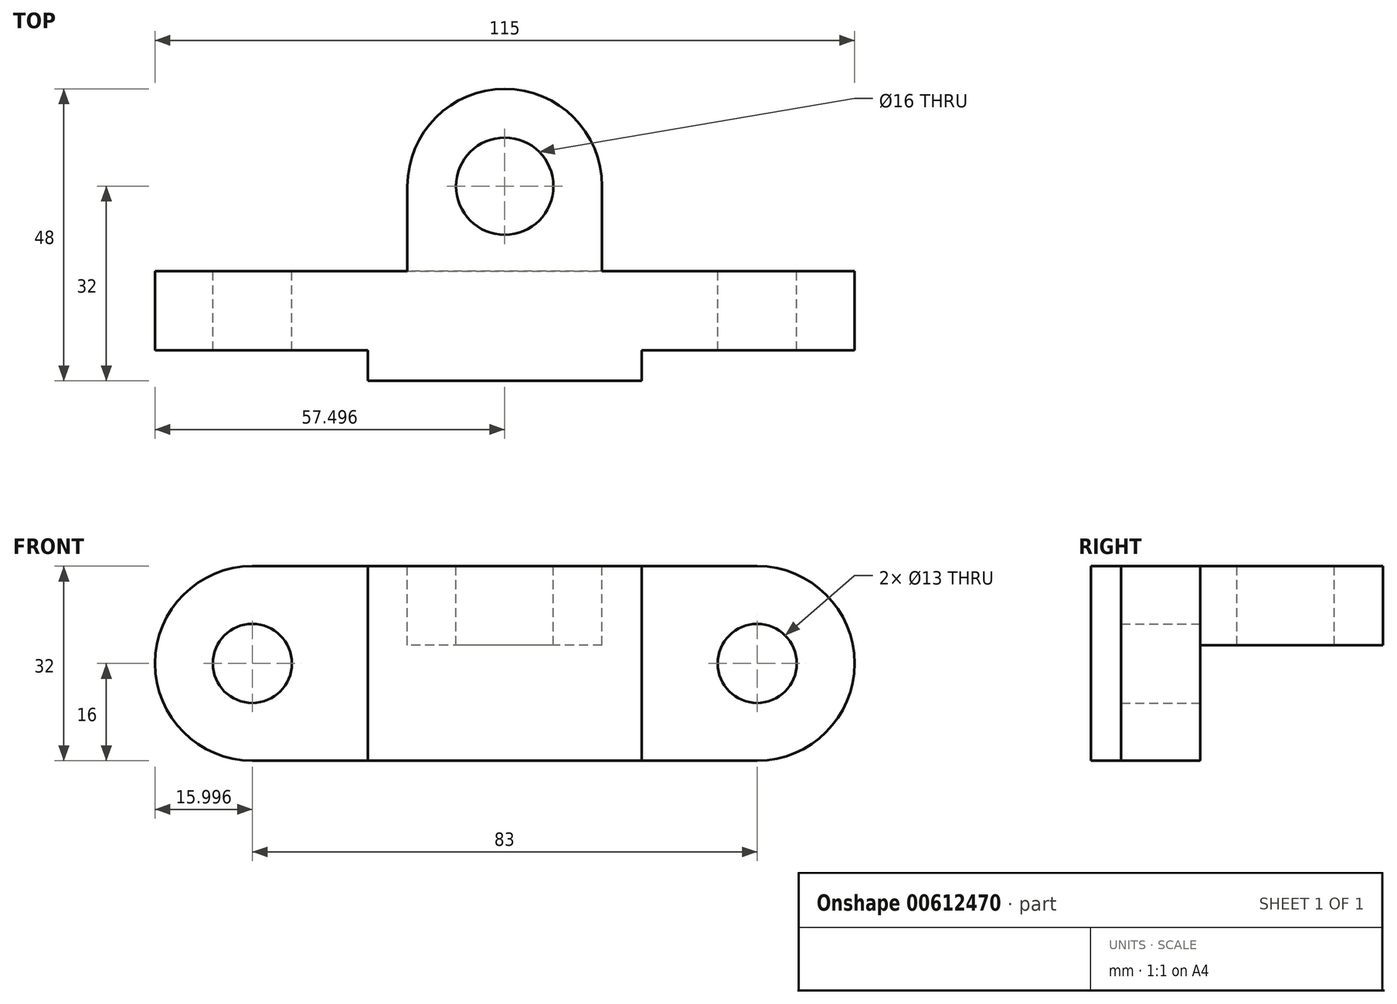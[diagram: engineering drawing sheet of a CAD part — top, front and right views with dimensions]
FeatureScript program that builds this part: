
annotation { "Feature Type Name" : "Feature", "Feature Type Description" : "" }
export const myFeature = defineFeature(function(context is Context, id is Id, definition is map)
    precondition{}
    {
        {
            var Q0;
            Q0=qCreatedBy(makeId("Front.planeOp"),FACE);
            var sketch = newSketch(context, id + "F0", { "sketchPlane" : qUnion([Q0])});
            skLineSegment(sketch, "E0", {"start": v(-60.04, 0) * mm, "end": v(22.96, 0) * mm});
            skLineSegment(sketch, "E1", {"start": v(22.96, 32) * mm, "end": v(-60.04, 32) * mm});
            skArc(sketch, "E2", {"start": v(-60.04, 32) * mm, "mid": v(-76.04, 16) * mm, "end": v(-60.04, 0) * mm});
            skArc(sketch, "E3", {"start": v(22.96, 32) * mm, "mid": v(38.96, 16) * mm, "end": v(22.96, 0) * mm});
            skCircle(sketch, "E4", {"center": v(22.96, 16) * mm, "radius": 6.5 * mm});
            skCircle(sketch, "E5", {"center": v(-60.04, 16) * mm, "radius": 6.5 * mm});
            skSolve(sketch);
        }
        {
            var Q0;
            Q0=makeQuery(id+"F0.imprint","IMPRINT",FACE,{"disambiguationData":[TD([[makeQuery(id+"F0.imprint","IMPRINT",EDGE,{"derivedFrom":sQuery(id+"F0.wireOp",EDGE,"E0")}),1.0]])]});
            extrude(context, id + "F1", {"entities" : qUnion([Q0]), "depth" : 13 * mm, "offsetDistance" : 25 * mm});
        }
        {
            var Q0;
            Q0=makeQuery(id+"F1.opExtrude","CAP_FACE",FACE,{"disambiguationData":[OSD([sQuery(id+"F0.wireOp",EDGE,"E0"),sQuery(id+"F0.wireOp",EDGE,"E1"),sQuery(id+"F0.wireOp",EDGE,"E2"),sQuery(id+"F0.wireOp",EDGE,"E3"),sQuery(id+"F0.wireOp",EDGE,"E4"),sQuery(id+"F0.wireOp",EDGE,"E5")])],"isStart":false});
            var sketch = newSketch(context, id + "F2", { "sketchPlane" : qUnion([Q0])});
            skLineSegment(sketch, "E6.bottom", {"start": v(-41.04, 32) * mm, "end": v(3.96, 32) * mm});
            skLineSegment(sketch, "E6.top", {"start": v(-41.04, 0) * mm, "end": v(3.96, 0) * mm});
            skLineSegment(sketch, "E6.left", {"start": v(-41.04, 32) * mm, "end": v(-41.04, 0) * mm});
            skLineSegment(sketch, "E6.right", {"start": v(3.96, 32) * mm, "end": v(3.96, 0) * mm});
            skLineSegment(sketch, "E7", {"start": v(-41.04, 16) * mm, "end": v(-60.04, 16) * mm, "construction": true});
            skLineSegment(sketch, "E8", {"start": v(3.96, 16) * mm, "end": v(22.96, 16) * mm, "construction": true});
            skSolve(sketch);
        }
        {
            var Q0;
            Q0=makeQuery(id+"F2.imprint","IMPRINT",FACE,{"disambiguationData":[TD([[makeQuery(id+"F2.imprint","IMPRINT",EDGE,{"derivedFrom":sQuery(id+"F2.wireOp",EDGE,"E6.bottom")}),1.0]])]});
            extrude(context, id + "F3", {"entities" : qUnion([Q0]), "operationType" : NewBodyOperationType.ADD, "depth" : 5 * mm, "offsetDistance" : 25 * mm});
        }
        {
            var Q0;
            Q0=makeQuery(id+"F3.boolean.opBoolean","MERGE",FACE,{"derivedFrom":[makeQuery(id+"F1.opExtrude","SWEPT_FACE",FACE,{"disambiguationData":[OSD([sQuery(id+"F0.wireOp",EDGE,"E1")])]}),makeQuery(id+"F3.opExtrude","SWEPT_FACE",FACE,{"disambiguationData":[OSD([sQuery(id+"F2.wireOp",EDGE,"E6.bottom")])]})]});
            var sketch = newSketch(context, id + "F4", { "sketchPlane" : qUnion([Q0])});
            skLineSegment(sketch, "E9.bottom", {"start": v(-34.54, 0) * mm, "end": v(-2.54, 0) * mm});
            skLineSegment(sketch, "E9.left", {"start": v(-34.54, 0) * mm, "end": v(-34.54, 14) * mm});
            skLineSegment(sketch, "E9.right", {"start": v(-2.54, 0) * mm, "end": v(-2.54, 14) * mm});
            skArc(sketch, "E10", {"start": v(-34.54, 14) * mm, "mid": v(-18.54, 30) * mm, "end": v(-2.54, 14) * mm});
            skCircle(sketch, "E11", {"center": v(-18.54, 14) * mm, "radius": 8 * mm});
            skSolve(sketch);
        }
        {
            var Q0;
            Q0=makeQuery(id+"F4.imprint","IMPRINT",FACE,{"disambiguationData":[TD([[makeQuery(id+"F4.imprint","IMPRINT",EDGE,{"derivedFrom":sQuery(id+"F4.wireOp",EDGE,"E9.bottom")}),-1.0]])]});
            extrude(context, id + "F5", {"entities" : qUnion([Q0]), "operationType" : NewBodyOperationType.ADD, "oppositeDirection" : true, "depth" : 13 * mm, "offsetDistance" : 25 * mm});
        }
    });
